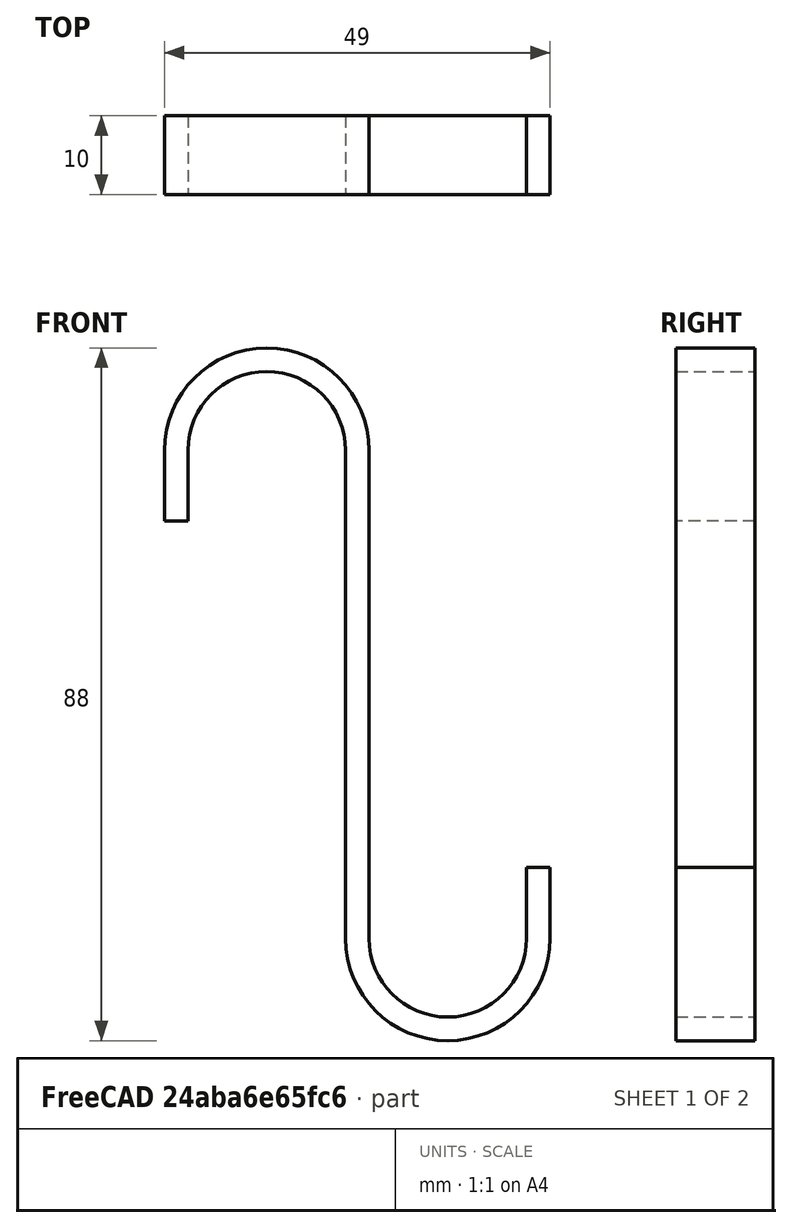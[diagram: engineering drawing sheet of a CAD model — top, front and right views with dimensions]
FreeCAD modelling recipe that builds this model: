
FCSTD DOCUMENT  (FreeCAD 0.16R6707 (Git))
Label: Gancho_Ikea
License: CreativeCommons Attribution-ShareAlike
LicenseURL: http://creativecommons.org/licenses/by-sa/4.0/
objects: Sketcher::SketchObject×1, PartDesign::Pad×1
note: 3 computed .brp shape members not serialized (recipe doc carries the construction recipe); baked Part::Feature solids carry a one-line shape summary decoded from their .brp

FEATURE [Sketcher::SketchObject] Sketch  label="BCT_Gancho"
  Placement = pos=(0,0,0) rot=(-1,0,0;4.71239rad)
  sketch-geometry (15):
    g0: LineSegment StartX=-21.5 StartY=31 StartZ=0 EndX=-21.5 EndY=22 EndZ=0
    g1: LineSegment StartX=-21.5 StartY=22 StartZ=0 EndX=-24.5 EndY=22 EndZ=0
    g2: LineSegment StartX=-24.5 StartY=22 StartZ=0 EndX=-24.5 EndY=31 EndZ=0
    g3: ArcOfCircle CenterX=-11.5 CenterY=31 CenterZ=0 NormalX=0 NormalY=0 NormalZ=1 Radius=10 StartAngle=0 EndAngle=3.14159
    g4: ArcOfCircle CenterX=-11.5 CenterY=31 CenterZ=0 NormalX=0 NormalY=0 NormalZ=1 Radius=13 StartAngle=0 EndAngle=3.14159
    g5: LineSegment StartX=-1.5 StartY=31 StartZ=0 EndX=-1.5 EndY=-31 EndZ=0
    g6: LineSegment StartX=1.5 StartY=31 StartZ=0 EndX=1.5 EndY=-31 EndZ=0
    g7: ArcOfCircle CenterX=11.5 CenterY=-31 CenterZ=0 NormalX=0 NormalY=0 NormalZ=1 Radius=10 StartAngle=3.14159 EndAngle=6.28319
    g8: ArcOfCircle CenterX=11.5 CenterY=-31 CenterZ=0 NormalX=0 NormalY=0 NormalZ=1 Radius=13 StartAngle=3.14159 EndAngle=6.28319
    g9: LineSegment StartX=21.5 StartY=-31 StartZ=0 EndX=21.5 EndY=-22 EndZ=0
    g10: LineSegment StartX=21.5 StartY=-22 StartZ=0 EndX=24.5 EndY=-22 EndZ=0
    g11: LineSegment StartX=24.5 StartY=-22 StartZ=0 EndX=24.5 EndY=-31 EndZ=0
    g12: LineSegment [constr] StartX=50.9518 StartY=31 StartZ=0 EndX=-51.5503 EndY=31 EndZ=0
    g13: LineSegment [constr] StartX=-51.8285 StartY=-31 StartZ=0 EndX=50.9518 EndY=-31 EndZ=0
    g14: LineSegment [constr] StartX=-1.5 StartY=-31 StartZ=0 EndX=1.5 EndY=-31 EndZ=0
  constraints (51):
    c: Equal(g1,g10)
    c: DistanceX(g1,g1) = 3
    c: Equal(g2,g0)
    c: Equal(g0,g9)
    c: Equal(g9,g11)
    c: DistanceY(g2,g2) = 9
    c: Equal(g4,g8)
    c: Radius(g4) = 13
    c: Parallel(g6,g5)
    c: Parallel(g5,g0)
    c: Parallel(g0,g2)
    c: Parallel(g2,g9)
    c: Parallel(g9,g11)
    c: Symmetric(g3,g4,g-2)
    c: Coincident(g7,g9)
    c: Coincident(g8,g11)
    c: Perpendicular(g-1,g2)
    c: Coincident(g0,g1)
    c: Coincident(g0,g3)
    c: Parallel(g13,g-1)
    c: Parallel(g12,g-1)
    c: PointOnObject(g3,g12)
    c: PointOnObject(g4,g12)
    c: PointOnObject(g8,g13)
    c: PointOnObject(g2,g12)
    c: PointOnObject(g4,g12)
    c: PointOnObject(g0,g12)
    c: PointOnObject(g5,g12)
    c: PointOnObject(g6,g12)
    c: PointOnObject(g5,g13)
    c: PointOnObject(g6,g13)
    c: PointOnObject(g7,g13)
    c: PointOnObject(g8,g13)
    c: PointOnObject(g7,g13)
    c: Coincident(g9,g10)
    c: Coincident(g10,g11)
    c: PointOnObject(g7,g13)
    c: PointOnObject(g8,g13)
    c: Coincident(g5,g8)
    c: Coincident(g6,g7)
    c: Coincident(g3,g5)
    c: Coincident(g4,g6)
    c: Coincident(g2,g4)
    c: Symmetric(g13,g12,g-1)
    c: Coincident(g1,g2)
    c: Coincident(g14,g5)
    c: Equal(g14,g1)
    c: Coincident(g6,g14)
    c: DistanceY(g-1,g1) = 22
    c: Parallel(g12,g13)
    c: Perpendicular(g-2,g12)
FEATURE [PartDesign::Pad] Pad  label="Gancho"
  Length = 10
  Length2 = 100
  Placement = pos=(0,0,0) rot=(-1,0,0;4.71239rad)
  Sketch = -> Sketch
  Type = 0
